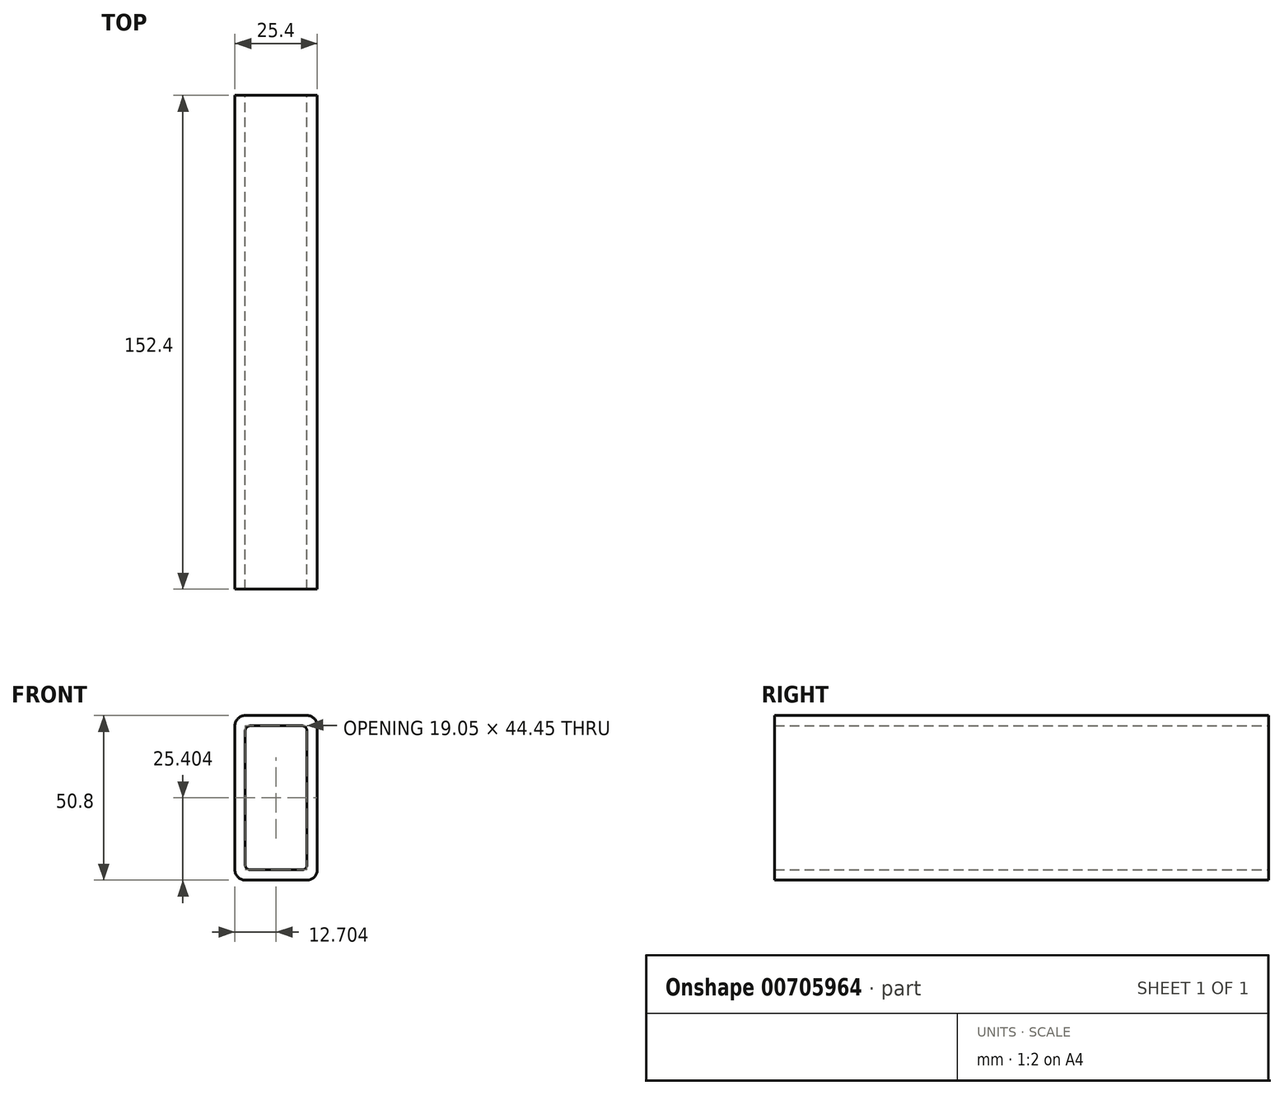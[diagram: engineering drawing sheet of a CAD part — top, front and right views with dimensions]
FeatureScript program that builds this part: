
annotation { "Feature Type Name" : "Feature", "Feature Type Description" : "" }
export const myFeature = defineFeature(function(context is Context, id is Id, definition is map)
    precondition{}
    {
        {
            var Q0;
            Q0=qCreatedBy(makeId("Front.planeOp"),FACE);
            var sketch = newSketch(context, id + "F0", { "sketchPlane" : qUnion([Q0])});
            skLineSegment(sketch, "E0.bottom", {"start": v(-19, 27.87) * mm, "end": v(6.4, 27.87) * mm});
            skLineSegment(sketch, "E0.top", {"start": v(-19, -22.93) * mm, "end": v(6.4, -22.93) * mm});
            skLineSegment(sketch, "E0.left", {"start": v(-19, 27.87) * mm, "end": v(-19, -22.93) * mm});
            skLineSegment(sketch, "E0.right", {"start": v(6.4, 27.87) * mm, "end": v(6.4, -22.93) * mm});
            skLineSegment(sketch, "E1.0", {"start": v(3.22, 24.7) * mm, "end": v(3.22, -19.75) * mm});
            skLineSegment(sketch, "E1.1", {"start": v(-15.83, 24.7) * mm, "end": v(3.22, 24.7) * mm});
            skLineSegment(sketch, "E1.2", {"start": v(-15.83, 24.7) * mm, "end": v(-15.83, -19.75) * mm});
            skLineSegment(sketch, "E1.3", {"start": v(-15.83, -19.75) * mm, "end": v(3.22, -19.75) * mm});
            skSolve(sketch);
        }
        {
            var Q0;
            Q0=makeQuery(id+"F0.imprint","IMPRINT",FACE,{"disambiguationData":[TD([[makeQuery(id+"F0.imprint","IMPRINT",EDGE,{"derivedFrom":sQuery(id+"F0.wireOp",EDGE,"E0.bottom")}),-1.0]])]});
            extrude(context, id + "F1", {"entities" : qUnion([Q0]), "depth" : 152.4 * mm, "offsetDistance" : 25.4 * mm});
        }
        {
            var Q0;
            Q0=makeQuery(id+"F1.opExtrude","SWEPT_EDGE",EDGE,{"disambiguationData":[OSD([sQuery(id+"F0.wireOp",EDGE,"E0.bottom"),sQuery(id+"F0.wireOp",EDGE,"E0.left")])]});
            var Q1;
            Q1=makeQuery(id+"F1.opExtrude","SWEPT_EDGE",EDGE,{"disambiguationData":[OSD([sQuery(id+"F0.wireOp",EDGE,"E0.bottom"),sQuery(id+"F0.wireOp",EDGE,"E0.right")])]});
            var Q2;
            Q2=makeQuery(id+"F1.opExtrude","SWEPT_EDGE",EDGE,{"disambiguationData":[OSD([sQuery(id+"F0.wireOp",EDGE,"E0.top"),sQuery(id+"F0.wireOp",EDGE,"E0.left")])]});
            var Q3;
            Q3=makeQuery(id+"F1.opExtrude","SWEPT_EDGE",EDGE,{"disambiguationData":[OSD([sQuery(id+"F0.wireOp",EDGE,"E0.top"),sQuery(id+"F0.wireOp",EDGE,"E0.right")])]});
            fillet(context, id + "F2", {"entities" : qUnion([Q0, Q1, Q2, Q3]), "radius" : 3.17 * mm, "tangentPropagation" : true, "allowEdgeOverflow" : false});
        }
        {
            var Q0;
            Q0=makeQuery(id+"F1.opExtrude","SWEPT_EDGE",EDGE,{"disambiguationData":[OSD([sQuery(id+"F0.wireOp",EDGE,"E1.1"),sQuery(id+"F0.wireOp",EDGE,"E1.2")])]});
            var Q1;
            Q1=makeQuery(id+"F1.opExtrude","SWEPT_EDGE",EDGE,{"disambiguationData":[OSD([sQuery(id+"F0.wireOp",EDGE,"E1.0"),sQuery(id+"F0.wireOp",EDGE,"E1.1")])]});
            var Q2;
            Q2=makeQuery(id+"F1.opExtrude","SWEPT_EDGE",EDGE,{"disambiguationData":[OSD([sQuery(id+"F0.wireOp",EDGE,"E1.0"),sQuery(id+"F0.wireOp",EDGE,"E1.3")])]});
            var Q3;
            Q3=makeQuery(id+"F1.opExtrude","SWEPT_EDGE",EDGE,{"disambiguationData":[OSD([sQuery(id+"F0.wireOp",EDGE,"E1.2"),sQuery(id+"F0.wireOp",EDGE,"E1.3")])]});
            fillet(context, id + "F3", {"entities" : qUnion([Q0, Q1, Q2, Q3]), "radius" : 1.52 * mm, "tangentPropagation" : true, "allowEdgeOverflow" : false});
        }
    });
